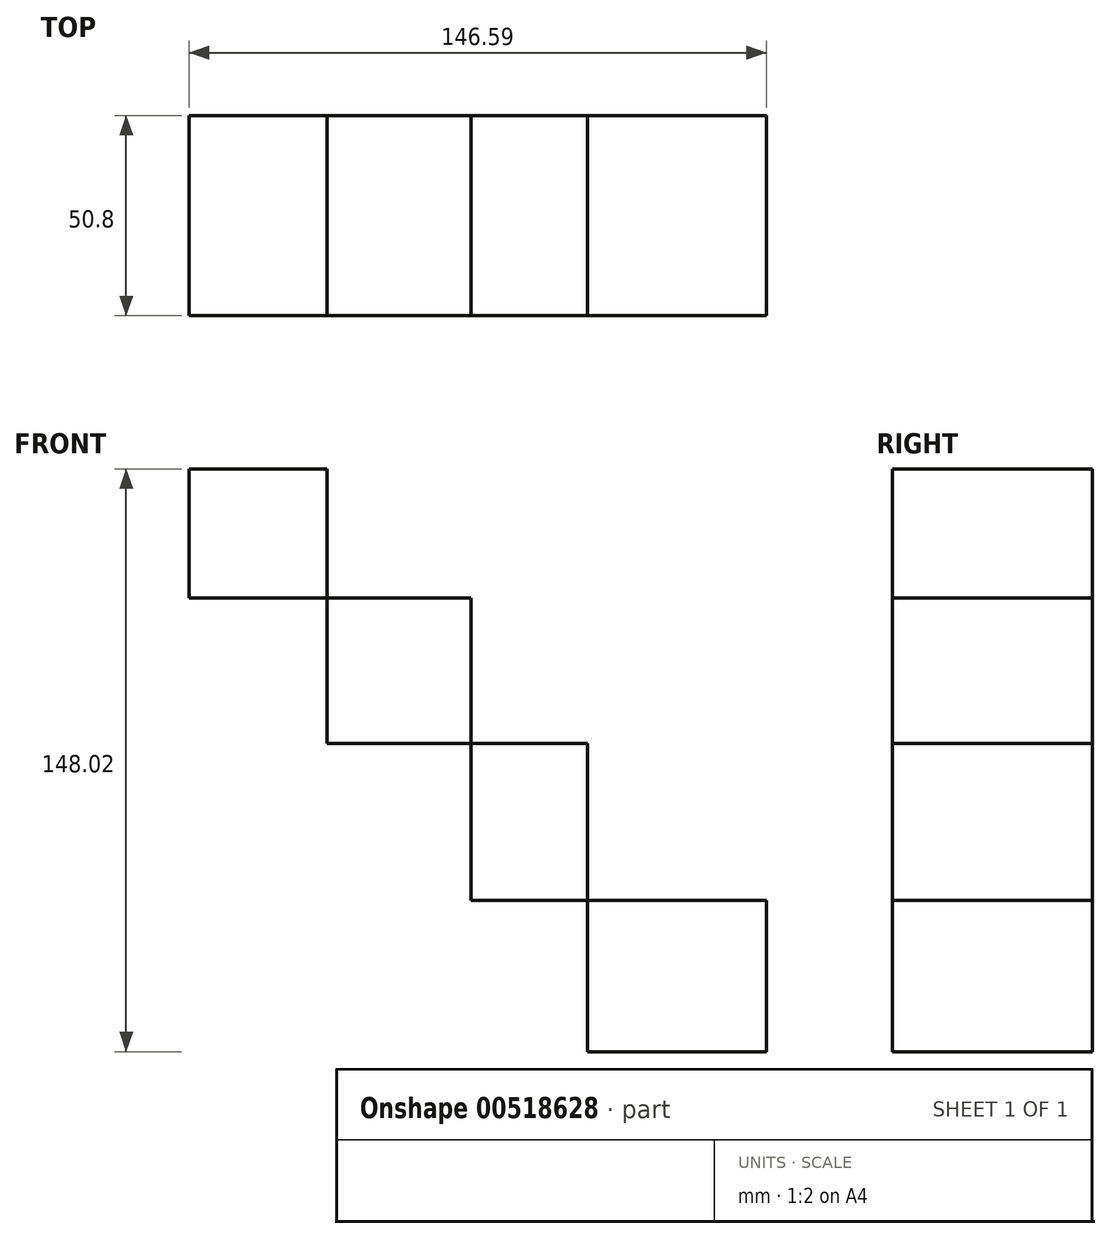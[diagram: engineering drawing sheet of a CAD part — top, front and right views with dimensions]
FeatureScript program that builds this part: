
annotation { "Feature Type Name" : "Feature", "Feature Type Description" : "" }
export const myFeature = defineFeature(function(context is Context, id is Id, definition is map)
    precondition{}
    {
        {
            var Q0;
            Q0=qCreatedBy(makeId("Front.planeOp"),FACE);
            var sketch = newSketch(context, id + "F0", { "sketchPlane" : qUnion([Q0])});
            skLineSegment(sketch, "E0.bottom", {"start": v(-79.38, 52.7) * mm, "end": v(-44.32, 52.7) * mm});
            skLineSegment(sketch, "E0.top", {"start": v(-79.38, 19.94) * mm, "end": v(-44.32, 19.94) * mm});
            skLineSegment(sketch, "E0.left", {"start": v(-79.38, 52.7) * mm, "end": v(-79.38, 19.94) * mm});
            skLineSegment(sketch, "E0.right", {"start": v(-44.32, 52.7) * mm, "end": v(-44.32, 19.94) * mm});
            skLineSegment(sketch, "E1.bottom", {"start": v(-44.32, 19.94) * mm, "end": v(-7.82, 19.94) * mm});
            skLineSegment(sketch, "E1.top", {"start": v(-44.32, -17.03) * mm, "end": v(-7.82, -17.03) * mm});
            skLineSegment(sketch, "E1.left", {"start": v(-44.32, 19.94) * mm, "end": v(-44.32, -17.03) * mm});
            skLineSegment(sketch, "E1.right", {"start": v(-7.82, 19.94) * mm, "end": v(-7.82, -17.03) * mm});
            skLineSegment(sketch, "E2.bottom", {"start": v(-7.82, -17.03) * mm, "end": v(21.73, -17.03) * mm});
            skLineSegment(sketch, "E2.top", {"start": v(-7.82, -56.88) * mm, "end": v(21.73, -56.88) * mm});
            skLineSegment(sketch, "E2.left", {"start": v(-7.82, -17.03) * mm, "end": v(-7.82, -56.88) * mm});
            skLineSegment(sketch, "E2.right", {"start": v(21.73, -17.03) * mm, "end": v(21.73, -56.88) * mm});
            skLineSegment(sketch, "E3.bottom", {"start": v(21.73, -56.88) * mm, "end": v(67.21, -56.88) * mm});
            skLineSegment(sketch, "E3.top", {"start": v(21.73, -95.32) * mm, "end": v(67.21, -95.32) * mm});
            skLineSegment(sketch, "E3.left", {"start": v(21.73, -56.88) * mm, "end": v(21.73, -95.32) * mm});
            skLineSegment(sketch, "E3.right", {"start": v(67.21, -56.88) * mm, "end": v(67.21, -95.32) * mm});
            skSolve(sketch);
        }
        {
            var Q0;
            Q0 = qSketchRegion(id + "F0", true);
            extrude(context, id + "F1", {"entities" : qUnion([Q0]), "depth" : 25.4 * mm, "offsetDistance" : 25.4 * mm});
        }
        {
            var Q0;
            Q0 = qSketchRegion(id + "F0", true);
            extrude(context, id + "F2", {"entities" : qUnion([Q0]), "operationType" : NewBodyOperationType.ADD, "oppositeDirection" : true, "depth" : 25.4 * mm, "offsetDistance" : 25.4 * mm});
        }
    });
